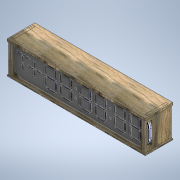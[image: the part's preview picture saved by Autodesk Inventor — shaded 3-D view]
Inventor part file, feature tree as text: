
AUTODESK INVENTOR PART (.ipt)
format: ipt  version: 2021 (Build 250183000, 183)  size: 3,488,256 bytes
history: native  units: in
note: dims shown in document units (in); Inventor stores cm internally (conversion verified against a paired STEP export)
features: other x71, extrude x17, sketch x16, imported_body x1
ambient origin geometry x8: Origin, YZ Plane, XZ Plane, XY Plane, X Axis, Y Axis, Z Axis, Center Point
bodies: Body1 (feature_tree), Body2 (feature_tree), Body3 (feature_tree), Body4 (feature_tree), Body5 (feature_tree), Body6 (feature_tree), Body7 (feature_tree)
feature tree (105):
  other  "Clock Face"
  other  "Blocks"
  extrude  "Extrusion1"  TaperAngle=135.0deg  [1 undecoded]
  extrude  "Extrusion3"  TaperAngle=135.0deg  [1 undecoded]
  extrude  "Extrusion5"  Depth=0.0433in
  extrude  "Extrusion6"  Depth=0.0433in
  extrude  "Extrusion9"  Depth=0.0433in
  extrude  "Extrusion7"  Depth=0.0433in
  extrude  "Extrusion10"  Depth=0.0433in
  extrude  "Extrusion8"  Depth=0.0433in
  extrude  "Extrusion13"  Depth=0.126in
  extrude  "Extrusion14"  Depth=0.126in
  extrude  "Extrusion15"  Depth=2.2441in
  extrude  "Extrusion16"  Depth=0.126in
  extrude  "Extrusion17"  Depth=0.126in
  extrude  "Extrusion18"  Depth=0.1969in
  extrude  "Extrusion19"  Depth=0.8661in
  extrude  "Extrusion20"  Depth=0.0866in
  extrude  "Extrusion21"  Depth=0.0118in
  other  "Single Segment"
  other  "7 Segment Digit"
  other  "Slanted Segment Large"
  other  "+ sign"
  other  "Dot"
  other  "Clock Face with T +-"
  other  "Clock Front Face Outline"
  other  "Small Segmemt"
  sketch  "Sketch5"  dims[d10=62.9921in d11=78.7402in d29=0.1181in d30=0.0in]
  sketch  "Sketch8"  dims[d105=0.0866in d108=0.0866in d111=0.0866in d112=0.0866in d113=0.0866in d114=0.0866in d115=0.0866in d116=0.0394in d117=0.1969in d121=0.0866in d122=0.0866in d126=135.0deg]
  other  "ClockBackface"
  sketch  "Sketch9"  dims[d127=0.8661in d128=135.0deg]
  sketch  "Sketch10"  dims[d129=0.0984in]
  other  "Backplace"
  sketch  "Sketch11"  dims[d131=0.0433in d132=0.0433in d137=0.0433in d138=0.0433in d139=0.0433in d140=0.0433in]
  other  "FrontCover"
  other  "7SegmentOutline"
  sketch  "Sketch15"  dims[d141=0.0433in d142=0.0433in]
  other  "Cable Trench"
  other  "Cable Trench Long"
  other  "CableCutouts"
  sketch  "Sketch17"  dims[d143=0.0433in d144=0.0433in]
  sketch  "Sketch20"  dims[d145=0.0433in d146=0.0433in]
  imported_body  "Base"
  sketch  "Sketch21"  dims[d150=0.0433in d151=0.0433in]
  other  "Side Panels"
  sketch  "Sketch22"  dims[d152=0.0433in d153=0.0433in]
  sketch  "Sketch23"  dims[d294=0.126in d295=0.126in]
  sketch  "Sketch25"  dims[d296=0.315in d297=0.126in]
  sketch  "Sketch26"  dims[d298=0.126in d299=2.2441in]
  other  "Top Panel"
  sketch  "Sketch27"  dims[d304=0.126in d305=0.126in]
  sketch  "Sketch28"  dims[d306=0.126in d307=0.126in]
  sketch  "Sketch29"  dims[d311=0.0787in d312=0.0787in d314=0.0787in d315=0.0787in d316=0.0787in d317=0.0787in d318=0.0787in d319=0.0787in d320=0.0394in d321=0.0394in d322=0.0394in d323=0.0394in d348=0.1969in d349=0.8661in d350=0.0866in d352=0.0118in d353=0.0118in d358=0.0118in d359=0.0118in d360=0.1969in d361=0.1969in d362=0.2953in d363=0.6693in d364=0.2953in d366=0.2953in d367=0.0in d368=0.0in d369=0.0in d370=0.0in d371=0.0in d372=0.5906in d373=0.0in d374=0.6299in d375=0.2362in d376=0.2362in d377=0.5354in d378=0.6299in d379=0.2362in d380=0.5906in d381=0.0in d402=1.9528in d429=12.9921in d430=2.7559in d431=0.9843in d462=0.0866in d463=0.0866in d464=0.0866in d465=0.0866in d466=0.0866in d467=0.0866in d468=0.0866in d469=0.0394in d470=0.1969in d471=0.0866in d472=0.0866in d473=135.0deg d474=0.6299in d475=135.0deg d476=0.0984in d477=0.1969in d478=0.6299in d479=0.0866in d480=0.0118in d481=0.0118in d482=0.0118in d483=0.0118in d496=0.0787in d497=0.0787in d501=0.0394in d502=0.0394in d503=0.0in d504=0.0in d505=0.039in d506=0.039in d507=0.039in d508=0.039in d509=0.8661in d510=0.9843in d511=0.9685in d514=0.0394in d515=0.0394in d516=0.0394in d517=0.0394in d518=0.0in d519=0.039in d520=0.4331in d522=0.9449in d523=0.0in d524=0.0591in d525=0.315in d526=0.2913in d527=0.8661in d528=0.6575in d529=0.315in d530=0.1969in d531=0.0in d536=1.378in d537=6.4961in d538=6.4961in d539=1.378in d542=1.378in d543=6.4961in d544=0.1181in d545=0.0in d549=0.1181in d550=0.0in d551=1.378in d552=6.4961in d553=0.1181in d554=0.0in d555=1.378in d556=6.4961in d557=0.1181in d558=0.0in d564=0.2362in d1135=1.1732in d1136=1.1732in d1137=2.1496in d1138=0.0612in d1139=0.0612in d1140=0.0612in d1143=0.0612in d1144=0.0612in d1145=90.0deg d1146=0.0866in d1147=0.0236in d1150=0.0236in d1153=0.0236in d1154=0.0866in d1155=1.0197in d1156=1.0197in d1157=0.0866in d1158=0.0236in d1159=0.0866in d1160=0.0866in d1161=0.0236in d1162=0.0866in d1163=0.0866in d1164=0.0236in d1165=0.0866in d1166=0.0866in d1167=0.0236in d1168=0.0866in d1169=0.0866in d1170=0.0866in d1171=0.0866in d1172=0.0866in d1173=0.0866in d1175=0.1102in d1176=0.8661in d1177=0.8661in d1178=1.0197in d1179=0.0866in d1180=0.0236in d1181=0.0866in d1182=0.0866in d1183=0.0236in d1184=0.0866in d1188=0.0866in d1189=0.0236in d1190=0.0866in d1193=0.0866in d1194=0.0236in d1195=0.0in d1196=0.0in d1198=135.0deg d1199=0.0612in d1200=0.0866in d1201=0.0in d1202=0.0in d1205=0.0in d1206=0.0in d1207=0.0in d1208=135.0deg d1209=90.0deg d1210=90.0deg d1211=0.0866in d1212=0.0236in d1213=0.6603in d1214=0.6603in d1215=0.6603in d1216=90.0deg d1217=135.0deg d1218=0.6603in d1219=0.0394in d1221=135.0deg d1222=0.0394in d1223=0.0866in d1224=0.0866in d1225=0.0866in d1227=0.0866in d1228=0.0866in d1229=0.0866in d1230=0.0236in d1231=135.0deg d1232=90.0deg d1233=90.0deg d1234=135.0deg d1235=90.0deg d1236=90.0deg d1239=0.1102in d1240=0.2402in d1241=0.2402in d1242=0.2835in d1243=0.2835in d1244=0.2402in d1245=0.2402in d1246=0.0669in d1247=0.0669in d1248=0.0669in d1249=0.0669in d1250=0.0433in d1251=0.0433in d1252=0.8661in d1253=0.1535in d1254=90.0deg d1255=135.0deg d1256=45.0deg d1257=0.6603in d1258=0.0236in d1259=135.0deg d1260=135.0deg d1261=90.0deg d1262=0.0612in d1263=0.0866in d1264=0.0in d1265=0.0in d1266=0.0in d1267=0.0in d1268=0.0in d1269=0.0in d1270=0.0in d1271=0.0in d1272=0.0in d1273=0.0in d1274=0.0in d1275=0.0in d1276=0.0in d1277=0.0in d1278=0.0in d1279=0.0in d1280=0.0in d1281=0.0in d1282=0.0in d1283=0.0in d1292=0.0866in d1307=0.0394in d1308=0.0394in d1309=0.0394in d1310=0.0394in d1311=0.0394in d1312=0.0394in d1313=0.0394in d1314=0.2756in d1315=0.0197in d1316=0.0197in d1317=0.3445in d1318=0.0394in d1319=0.0394in d1320=0.0787in d1321=0.0866in d1322=0.0787in d1323=0.0787in d1344=0.0394in d1350=0.0866in d1351=0.0866in d1386=0.1181in d1387=0.0in d1390=0.0394in d1392=0.0118in d1393=0.0394in d1394=0.0394in d1395=0.0394in d1396=0.0394in d1397=0.1378in d1398=0.1349in d1399=0.0394in d1402=0.0787in d1425=0.0in d1429=0.0in d1431=0.0394in d1432=0.0394in d1507=0.0in d1508=0.0394in d1509=0.0394in d1510=0.0394in d1511=0.0394in d1513=0.0394in d1514=0.0394in d1515=0.0in d1516=0.0in d1517=0.0in d1518=0.0in d1519=0.0197in d1520=0.0197in d1521=0.1969in d1522=0.0394in d1523=0.0394in d1524=0.0394in d1525=0.1181in d1526=0.1181in d1527=0.0394in d1529=0.2741in d1530=0.0787in d1531=0.0787in d1532=0.0325in d1533=0.033in d1534=0.0787in d1535=0.0787in d1536=0.0325in d1537=0.0787in d1538=0.0787in d1539=0.0325in d1635=0.0787in d1636=0.0689in d1638=0.2756in d1641=0.315in d1699=0.0197in d1700=0.0197in d1701=0.3445in d1702=0.0394in d1703=0.0394in d1704=0.0787in d1705=0.0787in d1706=0.0787in d1707=0.0in d1708=0.0394in d1709=0.0394in d1710=0.1462in d1711=0.0in d1712=0.0394in d1713=0.0394in d1714=0.0118in d1715=0.0394in d1716=0.0394in d1717=0.0394in d1718=0.0394in d1719=0.1378in d1720=0.1349in d1721=0.0394in d1722=0.0787in d1723=0.0787in d1724=0.0394in d1725=0.0394in d1726=0.0394in d1727=0.0394in d1728=0.0787in d1729=0.1181in d1730=0.0787in d1731=0.0394in d1732=0.0787in d1733=0.0787in d1734=0.0325in d1735=0.033in d1736=0.0787in d1737=0.0787in d1738=0.0325in d1739=0.0787in d1740=0.0787in d1741=0.0325in d1742=0.0325in d1747=0.2756in d1748=0.0984in d1749=0.0984in d1750=0.315in d1751=0.0325in d1752=0.0787in d1753=0.0787in d1754=0.0394in d1755=0.0394in d1756=0.0394in d1757=0.0394in d1758=0.0394in d1759=0.0394in d1760=0.0394in d1761=0.0394in d1762=0.0in d1763=0.0in d1764=0.0in d1765=0.0in d1766=0.0in d1767=0.0in d1768=0.0in d1769=0.0in d1770=0.1181in d1771=0.1181in d1772=0.4724in d1773=0.2362in d1774=0.0in d1775=0.0in d1776=0.0in d1777=0.0in d1778=0.0in d1779=0.0in d1780=0.0in d1781=0.0in d1782=0.2362in d1783=0.5906in d1784=0.1181in d1785=0.1181in d1786=0.0in d1787=0.0394in d1788=0.0394in d1789=0.0394in d1790=0.0394in d1791=0.0394in d1792=0.0394in d1793=0.0in d1794=0.0in d1795=0.0in d1796=0.0in d1797=0.0197in d1798=0.0197in d1799=0.1969in d1800=0.0394in d1801=0.0394in d1802=0.0394in d1803=0.1181in d1804=0.1181in d1805=0.0394in d1806=0.2741in d1808=0.0394in d1809=0.0394in d1810=0.0394in d1811=0.0394in d1812=0.0394in d1813=0.0394in d1814=0.0394in d1815=0.0394in d1840=0.0787in d1841=0.0787in d1842=0.501in d1843=0.0394in d1844=0.0394in d1845=90.0deg d1846=0.0in d1847=0.0in d1848=0.0in d1849=0.0in d1850=0.0in d1851=0.0in d1852=0.0in d1853=0.0in d1854=0.0in d1855=0.0in d1856=0.0in d1857=0.0in d1858=0.2756in d1859=0.0in d1860=0.0in d1861=0.0in d1862=0.2756in d1863=0.0in d1864=0.1181in d1865=0.0in d1898=0.0394in d1899=0.0591in d1900=0.0591in d1901=0.0591in d1902=0.0591in d1903=0.0591in d1904=0.0591in d1905=0.0394in d1906=0.2559in d1907=0.1772in d1908=0.1772in d1909=0.2559in d1910=0.1575in d1911=0.2362in d1912=0.2393in d1913=0.0197in d1914=0.3051in d1915=0.4066in d1916=0.3051in d1917=0.4066in d1918=0.0689in d1919=0.0689in d1920=0.0689in d1921=0.0in d1923=0.0335in d1924=0.0335in d1925=0.0335in d1926=0.0787in d1927=0.0335in d1940=0.2756in d1941=0.1181in d1942=0.1181in d1943=2.3622in d1944=0.1181in d1945=0.0in d1946=0.2362in d1948=0.0in d1949=0.0in d1950=0.2362in d1953=0.0in d1954=2.7559in d1955=0.0in d1956=0.1181in d1957=0.1181in d1958=0.2362in d1959=0.315in d1960=0.315in d1961=0.1181in d1962=0.2362in d1963=0.315in d1964=0.315in d1965=0.1181in d1966=0.2362in d1967=0.0in d1968=0.2362in d1969=0.315in d1970=0.315in d1971=0.0in d1972=0.0in d1973=0.2362in d1974=0.315in d1975=0.315in d1976=0.0in d1977=0.0in d1978=0.2362in d1979=0.0in d1980=0.0197in d1981=0.315in d1982=0.315in d1983=0.0in d1984=0.0in d1985=0.315in d1986=0.315in d1987=0.0in d1988=0.0in d1989=0.0197in d1990=0.2362in d1991=0.0in d1992=0.2362in d1993=0.0in d1994=0.2362in d1995=0.0in d1996=0.315in d1997=0.315in d1998=0.2362in d1999=0.0in d2000=0.315in d2001=0.315in d2002=0.2362in d2003=0.0in d2004=0.0in d2006=0.3386in d2007=0.3386in d2008=0.2362in d2009=0.0in d2010=0.0in d2011=0.3386in d2012=0.3386in d2013=0.0in d2014=0.0in d2015=0.2362in d2016=0.0in d2017=0.0in d2018=0.0in d2019=0.0in d2020=0.0in]
  other  "Single Segment:9"
  other  "Single Segment:10"
  other  "Single Segment:11"
  other  "Single Segment:12"
  other  "Single Segment:13"
  other  "Single Segment:14"
  other  "Single Segment:15"
  other  "7 Segment Digit:8"
  other  "7 Segment Digit:9"
  other  "7 Segment Digit:10"
  other  "7 Segment Digit:11"
  other  "7 Segment Digit:12"
  other  "7 Segment Digit:13"
  other  "Dot:7"
  other  "Dot:8"
  other  "Dot:9"
  other  "Dot:10"
  other  "Clock Front Face Outline:1"
  other  "Small Segmemt:1"
  other  "Small Segmemt:2"
  other  "Small Segmemt:3"
  other  "Small Segmemt:4"
  other  "+ sign:1"
  other  "Small Segmemt:5"
  other  "Small Segmemt:6"
  other  "Small Segmemt:7"
  other  "Small Segmemt:8"
  other  "Clock Face with T +-:1"
  other  "Clock Front Face Outline:2"
  other  "Clock Front Face Outline:3"
  other  "Clock Front Face Outline:4"
  other  "7SegmentOutline:1"
  other  "7SegmentOutline:2"
  other  "7SegmentOutline:3"
  other  "7SegmentOutline:4"
  other  "7SegmentOutline:5"
  other  "7SegmentOutline:6"
  other  "Dot:11"
  other  "Dot:12"
  other  "Dot:13"
  other  "Dot:14"
  other  "Cable Trench:3"
  other  "Cable Trench:4"
  other  "Cable Trench:5"
  other  "Cable Trench Long:4"
  other  "Cable Trench Long:5"
  other  "CableCutouts:3"
  other  "CableCutouts:4"
  other  "CableCutouts:5"
  other  "CableCutouts:6"
  other  "CableCutouts:7"
  other  "CableCutouts:8"
note: 2 required parameter values undecoded (feature->parameter linkage not recoverable at this tier; creation-order binding heuristic only, values carry confidence <= 0.55)
